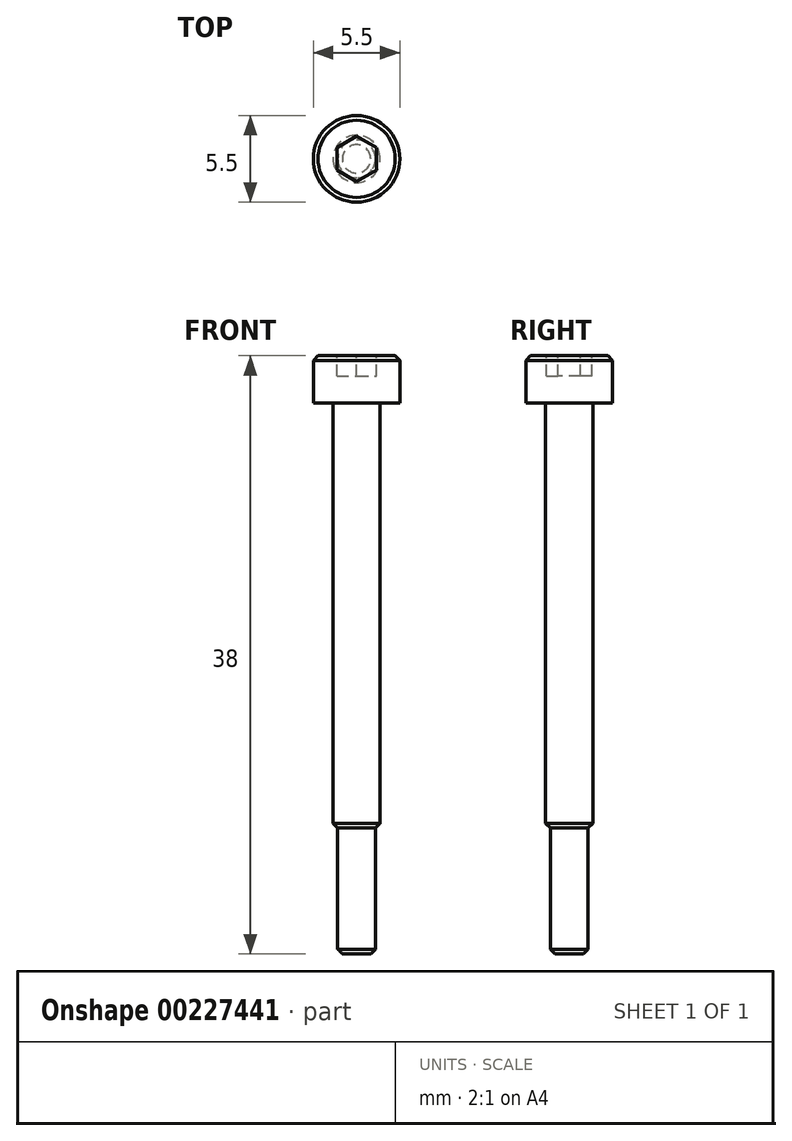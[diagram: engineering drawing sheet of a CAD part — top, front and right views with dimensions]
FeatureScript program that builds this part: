
annotation { "Feature Type Name" : "Feature", "Feature Type Description" : "" }
export const myFeature = defineFeature(function(context is Context, id is Id, definition is map)
    precondition{}
    {
        {
            assignVariable(context, id + "F0", {"name" : "M", "anyValue" : 3});
        }
        {
            assignVariable(context, id + "F1", {"name" : "length", "anyValue" : 35});
        }
        {
            assignVariable(context, id + "F2", {"name" : "length_thread", "anyValue" : 8});
        }
        {
            var Q0;
            Q0=qCreatedBy(makeId("Top.planeOp"),FACE);
            var sketch = newSketch(context, id + "F3", { "sketchPlane" : qUnion([Q0])});
            skCircle(sketch, "E0", {"center": v(0, 0) * mm, "radius": 1.5 * mm});
            skCircle(sketch, "E1", {"center": v(0, 0) * mm, "radius": 2.75 * mm});
            skSolve(sketch);
        }
        {
            var Q0;
            Q0=makeQuery(id+"F3.imprint","IMPRINT",FACE,{"disambiguationData":[TD([[makeQuery(id+"F3.imprint","IMPRINT",EDGE,{"derivedFrom":sQuery(id+"F3.wireOp",EDGE,"E0")}),1.0]])]});
            extrude(context, id + "F4", {"entities" : qUnion([Q0]), "oppositeDirection" : true, "depth" : (getVariable(context, 'length') - getVariable(context, 'length_thread')) * mm});
        }
        {
            var Q0;
            Q0=makeQuery(id+"F4.opExtrude","CAP_FACE",FACE,{"disambiguationData":[OSD([sQuery(id+"F3.wireOp",EDGE,"E0")])],"isStart":false});
            var sketch = newSketch(context, id + "F5", { "sketchPlane" : qUnion([Q0])});
            skCircle(sketch, "E2", {"center": v(0, 0) * mm, "radius": 1.2 * mm});
            skSolve(sketch);
        }
        {
            var Q0;
            Q0=makeQuery(id+"F5.imprint","IMPRINT",FACE,{"disambiguationData":[TD([[makeQuery(id+"F5.imprint","IMPRINT",EDGE,{"derivedFrom":sQuery(id+"F5.wireOp",EDGE,"E2")}),1.0]])]});
            extrude(context, id + "F6", {"entities" : qUnion([Q0]), "operationType" : NewBodyOperationType.ADD, "depth" : (getVariable(context, 'length_thread')) * mm});
        }
        {
            var Q0;
            Q0 = qSketchRegion(id + "F3", true);
            var Q1;
            Q1=makeQuery(id+"F4.opExtrude","CAP_FACE",FACE,{"disambiguationData":[OSD([sQuery(id+"F3.wireOp",EDGE,"E0")])],"isStart":true});
            extrude(context, id + "F7", {"entities" : qUnion([Q0, Q1]), "operationType" : NewBodyOperationType.ADD, "depth" : (getVariable(context, 'M')) * mm});
        }
        {
            var Q0;
            Q0=makeQuery(id+"F4.opExtrude","CAP_EDGE",EDGE,{"disambiguationData":[OSD([sQuery(id+"F3.wireOp",EDGE,"E0")])],"isStart":false});
            var Q1;
            Q1=makeQuery(id+"F7.opExtrude","CAP_EDGE",EDGE,{"disambiguationData":[OSD([sQuery(id+"F3.wireOp",EDGE,"E1")])],"isStart":false});
            var Q2;
            Q2=makeQuery(id+"F6.opExtrude","CAP_EDGE",EDGE,{"disambiguationData":[OSD([sQuery(id+"F5.wireOp",EDGE,"E2")])],"isStart":false});
            chamfer(context, id + "F8", {"entities" : qUnion([Q0, Q1, Q2]), "width" : 0.3 * mm, "tangentPropagation" : true});
        }
        {
            var Q0;
            {var subQ0=sQuery(id+"F3.wireOp",EDGE,"E0");Q0=makeQuery(id+"F7.boolean.opBoolean","MERGE",FACE,{"derivedFrom":[makeQuery(id+"F7.opExtrude","CAP_FACE",FACE,{"disambiguationData":[OSD([subQ0,sQuery(id+"F3.wireOp",EDGE,"E1")])],"isStart":false}),makeQuery(id+"F7.opExtrude","CAP_FACE",FACE,{"disambiguationData":[OSD([subQ0])],"isStart":false})]});}
            var sketch = newSketch(context, id + "F9", { "sketchPlane" : qUnion([Q0])});
            skCircle(sketch, "E3.cCircle", {"center": v(0, 0) * mm, "radius": 1.25 * mm, "construction": true});
            skLineSegment(sketch, "E3.0", {"start": v(1.25, 0.72) * mm, "end": v(1.25, -0.72) * mm});
            skLineSegment(sketch, "E3.1", {"start": v(1.25, -0.72) * mm, "end": v(0, -1.44) * mm});
            skLineSegment(sketch, "E3.2", {"start": v(0, -1.44) * mm, "end": v(-1.25, -0.72) * mm});
            skLineSegment(sketch, "E3.3", {"start": v(-1.25, -0.72) * mm, "end": v(-1.25, 0.72) * mm});
            skLineSegment(sketch, "E3.4", {"start": v(-1.25, 0.72) * mm, "end": v(0, 1.44) * mm});
            skLineSegment(sketch, "E3.5", {"start": v(0, 1.44) * mm, "end": v(1.25, 0.72) * mm});
            skPoint(sketch, "E3.0.midPoint", {"position": v(1.25, 0) * mm});
            skSolve(sketch);
        }
        {
            var Q0;
            Q0=makeQuery(id+"F9.imprint","IMPRINT",FACE,{"disambiguationData":[TD([[makeQuery(id+"F9.imprint","IMPRINT",EDGE,{"derivedFrom":sQuery(id+"F9.wireOp",EDGE,"E3.0")}),-1.0]])]});
            extrude(context, id + "F10", {"entities" : qUnion([Q0]), "operationType" : NewBodyOperationType.REMOVE, "oppositeDirection" : true, "depth" : 1.3 * mm});
        }
    });
